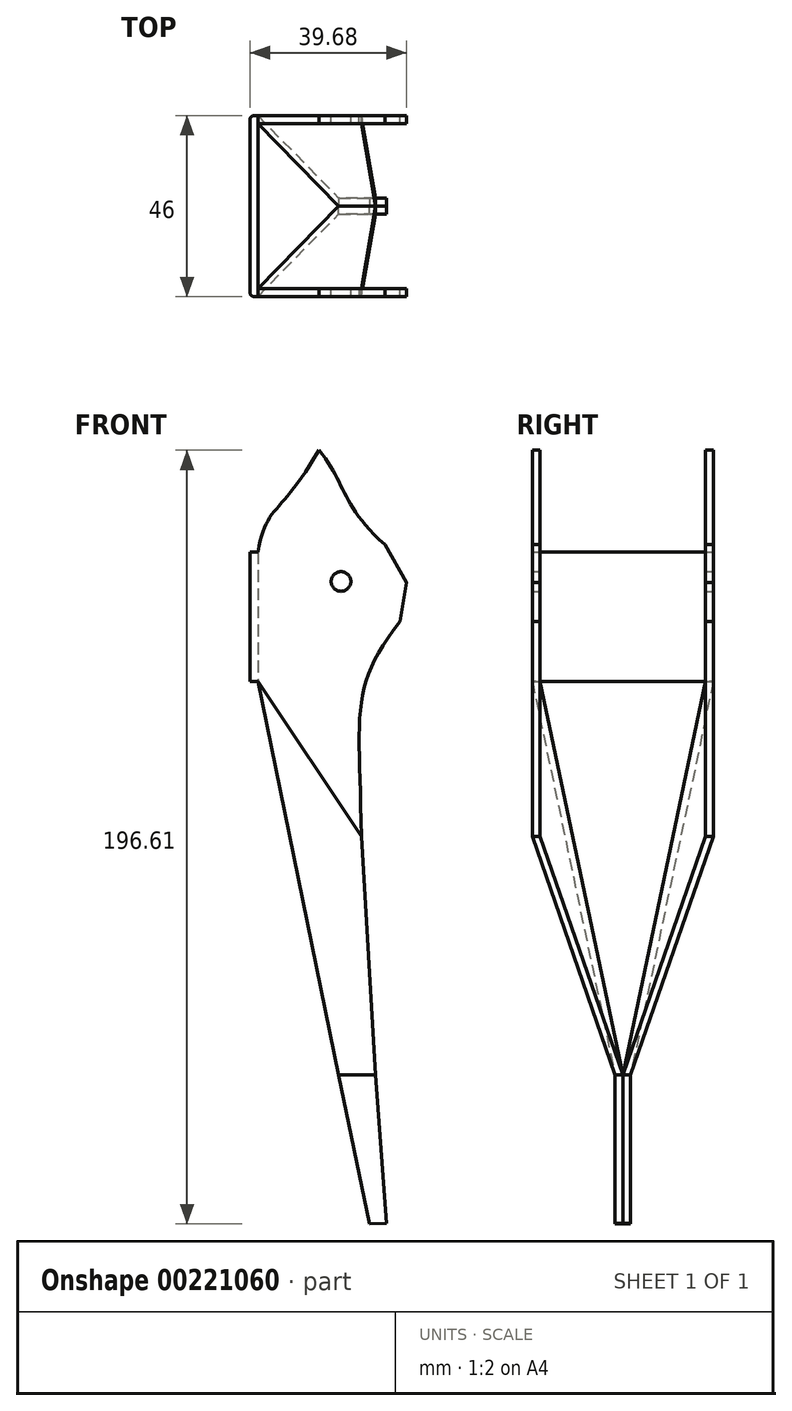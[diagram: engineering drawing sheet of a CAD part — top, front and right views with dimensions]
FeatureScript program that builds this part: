
annotation { "Feature Type Name" : "Feature", "Feature Type Description" : "" }
export const myFeature = defineFeature(function(context is Context, id is Id, definition is map)
    precondition{}
    {
        {
            var Q0;
            Q0=qCreatedBy(makeId("Front.planeOp"),FACE);
            var sketch = newSketch(context, id + "F0", { "sketchPlane" : qUnion([Q0])});
            skLineSegment(sketch, "E0", {"start": v(-57.44, 5.36) * mm, "end": v(-29.1, -132.47) * mm});
            skCircle(sketch, "E1", {"center": v(-36.31, 30.77) * mm, "radius": 2.5 * mm});
            skLineSegment(sketch, "E2", {"start": v(-57.44, 38.23) * mm, "end": v(-57.44, 5.36) * mm});
            skLineSegment(sketch, "E3", {"start": v(-25.18, 40.15) * mm, "end": v(-19.72, 30.45) * mm});
            skLineSegment(sketch, "E4", {"start": v(-57.44, 38.23) * mm, "end": v(-59.4, 38.23) * mm});
            skLineSegment(sketch, "E5", {"start": v(-59.4, 38.23) * mm, "end": v(-59.4, 5.36) * mm});
            skLineSegment(sketch, "E6", {"start": v(-59.4, 5.36) * mm, "end": v(-57.44, 5.36) * mm});
            skLineSegment(sketch, "E7", {"start": v(-19.72, 30.45) * mm, "end": v(-21.3, 20.58) * mm});
            skFitSpline(sketch, "E8", {"points": [v(-21.3, 20.58) * mm, v(-31.14, -35.38) * mm], "startDerivative": vector(-39.68, -51.32) * mm, "endDerivative": vector(1.08, -100.07) * mm});
            skLineSegment(sketch, "E9", {"start": v(-31.7, -35.74) * mm, "end": v(-24.78, -132.25) * mm});
            skLineSegment(sketch, "E10", {"start": v(-29.1, -132.47) * mm, "end": v(-24.78, -132.25) * mm});
            skLineSegment(sketch, "E11", {"start": v(-57.44, 5.36) * mm, "end": v(-31.15, -34.06) * mm});
            skFitSpline(sketch, "E12", {"points": [v(-41.94, 64.14) * mm, v(-25.18, 40.15) * mm], "startDerivative": vector(21.16, -25.4) * mm, "endDerivative": vector(34.39, -30.69) * mm});
            skFitSpline(sketch, "E13", {"points": [v(-41.94, 64.14) * mm, v(-57.44, 38.23) * mm], "startDerivative": vector(-28.04, -49.2) * mm, "endDerivative": vector(-6.11, -36.58) * mm});
            skPoint(sketch, "E14.start.orphan", {"position": v(-38.83, -85.11) * mm});
            skPoint(sketch, "E15.end.orphan", {"position": v(-38.83, -81.77) * mm});
            skLineSegment(sketch, "E16", {"start": v(-27.49, -94.54) * mm, "end": v(-36.9, -94.54) * mm});
            skLineSegment(sketch, "E17", {"start": v(-36.9, -94.54) * mm, "end": v(-37.3, -92.54) * mm});
            skLineSegment(sketch, "E18", {"start": v(-37.3, -92.54) * mm, "end": v(-27.63, -92.54) * mm});
            skSolve(sketch);
        }
        {
            var Q0;
            {var subQ0=sQuery(id+"F0.wireOp",EDGE,"E10");Q0=makeQuery(id+"F0.imprint","IMPRINT",FACE,{"disambiguationData":[TD([[makeQuery(id+"F0.imprint","IMPRINT",EDGE,{"derivedFrom":subQ0}),1.0]])]});}
            extrude(context, id + "F1", {"entities" : qUnion([Q0]), "oppositeDirection" : true, "depth" : 2 * mm});
        }
        {
            var Q0;
            Q0=makeQuery(id+"F0.imprint","IMPRINT",FACE,{"disambiguationData":[TD([[makeQuery(id+"F0.imprint","IMPRINT",EDGE,{"derivedFrom":sQuery(id+"F0.wireOp",EDGE,"E1")}),-1.0]])]});
            var Q1;
            Q1=makeQuery(id+"F0.imprint","IMPRINT",FACE,{"disambiguationData":[TD([[makeQuery(id+"F0.imprint","IMPRINT",EDGE,{"derivedFrom":sQuery(id+"F0.wireOp",EDGE,"E2")}),-1.0]])]});
            extrude(context, id + "F2", {"entities" : qUnion([Q0, Q1]), "endBound" : BoundingType.SYMMETRIC, "depth" : 46 * mm});
        }
        {
            var Q0;
            Q0=makeQuery(id+"F0.imprint","IMPRINT",FACE,{"disambiguationData":[TD([[makeQuery(id+"F0.imprint","IMPRINT",EDGE,{"derivedFrom":sQuery(id+"F0.wireOp",EDGE,"E1")}),-1.0]])]});
            extrude(context, id + "F3", {"entities" : qUnion([Q0]), "operationType" : NewBodyOperationType.REMOVE, "endBound" : BoundingType.SYMMETRIC, "depth" : 42 * mm});
        }
        {
            var Q0;
            {var subQ0=sQuery(id+"F0.wireOp",EDGE,"E13");var subQ1=sQuery(id+"F0.wireOp",EDGE,"E12");var subQ2=sQuery(id+"F0.wireOp",EDGE,"E11");var subQ3=sQuery(id+"F0.wireOp",EDGE,"E8");var subQ4=sQuery(id+"F0.wireOp",EDGE,"E7");var subQ5=sQuery(id+"F0.wireOp",EDGE,"E3");var subQ6=sQuery(id+"F0.wireOp",EDGE,"E2");var subQ7=sQuery(id+"F0.wireOp",EDGE,"E1");Q0=makeQuery(id+"F3.boolean.opBoolean","SPLIT",FACE,{"disambiguationData":[TD([makeQuery(id+"F3.opExtrude","CAP_FACE",FACE,{"disambiguationData":[OSD([subQ7,subQ6,subQ5,subQ4,subQ3,subQ2,subQ1,subQ0])],"isStart":true})])],"derivedFrom":makeQuery(id+"F2.opExtrude","SWEPT_FACE",FACE,{"disambiguationData":[OSD([subQ2])]})});}
            var Q1;
            {var subQ0=sQuery(id+"F0.wireOp",EDGE,"E9");var subQ1=sQuery(id+"F0.wireOp",EDGE,"E16");var subQ2=sQuery(id+"F0.wireOp",EDGE,"E0");Q1=makeQuery(id+"FlpuHt3dEil0ecl_2.boolean.opBoolean","SPLIT",FACE,{"disambiguationData":[TD([makeQuery(id+"F1.opExtrude","CAP_FACE",FACE,{"disambiguationData":[OSD([subQ2,subQ0,sQuery(id+"F0.wireOp",EDGE,"E10"),subQ1])],"isStart":true})])],"derivedFrom":makeQuery(id+"F1.opExtrude","SWEPT_FACE",FACE,{"disambiguationData":[OSD([subQ1])]})});}
            loft(context, id + "F4", {"sheetProfilesArray" : [{ "sheetProfileEntities" : qUnion([Q0]) }, { "sheetProfileEntities" : qUnion([Q1]) }]});
        }
        {
            var Q0;
            {var subQ0=sQuery(id+"F0.wireOp",EDGE,"E10");Q0=makeQuery(id+"F0.imprint","IMPRINT",FACE,{"disambiguationData":[TD([[makeQuery(id+"F0.imprint","IMPRINT",EDGE,{"derivedFrom":subQ0}),1.0]])]});}
            extrude(context, id + "F5", {"entities" : qUnion([Q0]), "depth" : 2 * mm});
        }
        {
            var Q0;
            {var subQ0=sQuery(id+"F0.wireOp",EDGE,"E8");var subQ1=sQuery(id+"F0.wireOp",EDGE,"E13");var subQ2=sQuery(id+"F0.wireOp",EDGE,"E12");var subQ3=sQuery(id+"F0.wireOp",EDGE,"E11");var subQ4=sQuery(id+"F0.wireOp",EDGE,"E7");var subQ5=sQuery(id+"F0.wireOp",EDGE,"E3");var subQ6=sQuery(id+"F0.wireOp",EDGE,"E2");var subQ7=sQuery(id+"F0.wireOp",EDGE,"E1");Q0=makeQuery(id+"F3.boolean.opBoolean","SPLIT",FACE,{"disambiguationData":[TD([makeQuery(id+"F3.opExtrude","CAP_FACE",FACE,{"disambiguationData":[OSD([subQ7,subQ6,subQ5,subQ4,subQ0,subQ3,subQ2,subQ1])],"isStart":false})])],"derivedFrom":makeQuery(id+"F2.opExtrude","SWEPT_FACE",FACE,{"disambiguationData":[OSD([subQ3])]})});}
            var Q1;
            Q1=makeQuery(id+"F5.opExtrude","SWEPT_FACE",FACE,{"disambiguationData":[OSD([sQuery(id+"F0.wireOp",EDGE,"E16")])]});
            loft(context, id + "F6", {"sheetProfilesArray" : [{ "sheetProfileEntities" : qUnion([Q0]) }, { "sheetProfileEntities" : qUnion([Q1]) }]});
        }
        {
            var Q0;
            Q0=makeQuery(id+"F2.opExtrude","CAP_EDGE",EDGE,{"disambiguationData":[OSD([sQuery(id+"F0.wireOp",EDGE,"E5")])],"isStart":false});
            fillet(context, id + "F7", {"entities" : qUnion([Q0]), "radius" : 1 * mm, "tangentPropagation" : true, "allowEdgeOverflow" : false});
        }
        {
            var Q0;
            Q0=makeQuery(id+"F2.opExtrude","CAP_EDGE",EDGE,{"disambiguationData":[OSD([sQuery(id+"F0.wireOp",EDGE,"E5")])],"isStart":true});
            fillet(context, id + "F8", {"entities" : qUnion([Q0]), "radius" : 1 * mm, "tangentPropagation" : true, "allowEdgeOverflow" : false});
        }
    });
